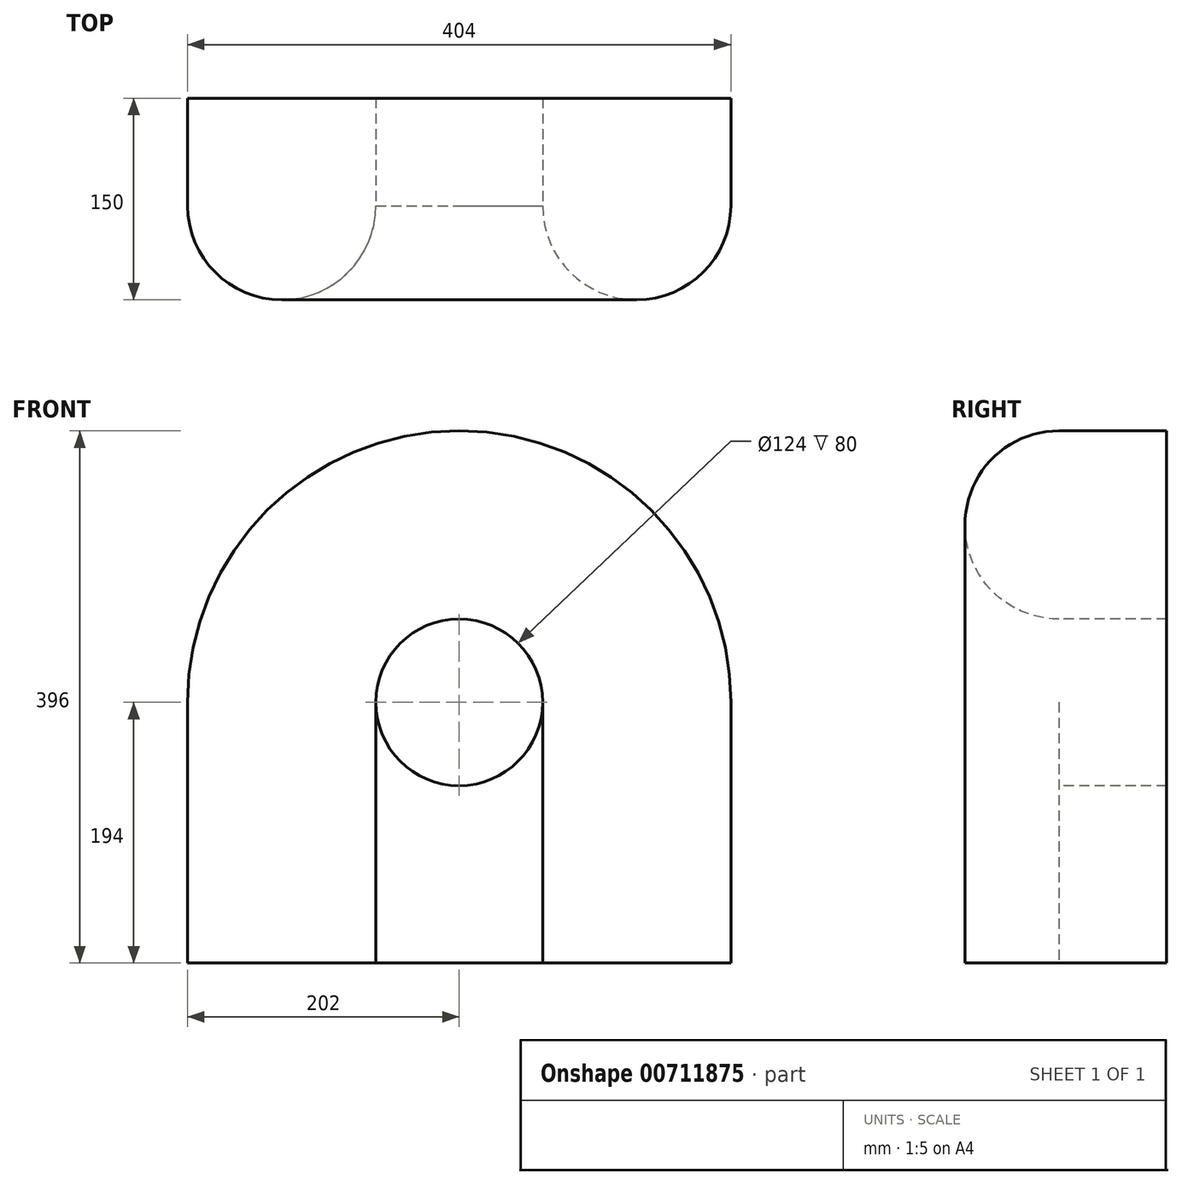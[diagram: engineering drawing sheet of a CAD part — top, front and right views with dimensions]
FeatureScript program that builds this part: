
annotation { "Feature Type Name" : "Feature", "Feature Type Description" : "" }
export const myFeature = defineFeature(function(context is Context, id is Id, definition is map)
    precondition{}
    {
        {
            var Q0;
            Q0=qCreatedBy(makeId("Front.planeOp"),FACE);
            var sketch = newSketch(context, id + "F0", { "sketchPlane" : qUnion([Q0])});
            skLineSegment(sketch, "E0.left", {"start": v(64, 0) * mm, "end": v(64, 194) * mm});
            skLineSegment(sketch, "E0.right", {"start": v(-200, 0) * mm, "end": v(-200, 194) * mm});
            skArc(sketch, "E1", {"start": v(64, 194) * mm, "mid": v(-68, 326) * mm, "end": v(-200, 194) * mm});
            skPoint(sketch, "E1.centerSnap0", {"position": v(-68, 194) * mm});
            skSolve(sketch);
        }
        {
            var Q0;
            Q0=qCreatedBy(makeId("Top.planeOp"),FACE);
            var sketch = newSketch(context, id + "F1", { "sketchPlane" : qUnion([Q0])});
            skCircle(sketch, "E2", {"center": v(64, 0) * mm, "radius": 70 * mm});
            skSolve(sketch);
        }
        {
            var Q0;
            Q0=qCreatedBy(makeId("Front.planeOp"),FACE);
            var sketch = newSketch(context, id + "F2", { "sketchPlane" : qUnion([Q0])});
            skCircle(sketch, "E3", {"center": v(-68, 194) * mm, "radius": 202 * mm});
            skLineSegment(sketch, "E4.bottom", {"start": v(-270, 194) * mm, "end": v(134, 194) * mm});
            skLineSegment(sketch, "E4.top", {"start": v(-270, -18.77) * mm, "end": v(134, -18.77) * mm});
            skLineSegment(sketch, "E4.left", {"start": v(-270, 194) * mm, "end": v(-270, -18.77) * mm});
            skLineSegment(sketch, "E4.right", {"start": v(134, 194) * mm, "end": v(134, -18.77) * mm});
            skSolve(sketch);
        }
        {
            var Q0;
            Q0=makeQuery(id+"F1.imprint","IMPRINT",FACE,{"disambiguationData":[TD([[makeQuery(id+"F1.imprint","IMPRINT",EDGE,{"derivedFrom":sQuery(id+"F1.wireOp",EDGE,"E2")}),1.0]])]});
            var Q1;
            Q1=sQuery(id+"F0.wireOp",EDGE,"E0.left");
            var Q2;
            Q2=sQuery(id+"F0.wireOp",EDGE,"E1");
            var Q3;
            Q3=sQuery(id+"F0.wireOp",EDGE,"E0.right");
            sweep(context, id + "F3", {"profiles" : qUnion([Q0]), "path" : qUnion([Q1, Q2, Q3])});
        }
        {
            var Q0;
            {var subQ0=sQuery(id+"F2.wireOp",EDGE,"E4.bottom");var subQ1=sQuery(id+"F2.wireOp",EDGE,"E3");var subQ3=makeQuery(id+"F2.imprint","INTERSECT",VERTEX,{"derivedFrom":[subQ1,subQ0]});Q0=makeQuery(id+"F2.imprint","IMPRINT",FACE,{"disambiguationData":[TD([[makeQuery(id+"F2.imprint","IMPRINT",EDGE,{"disambiguationData":[TD([[subQ3,-1.0]])],"derivedFrom":subQ1}),1.0]])]});}
            var Q1;
            {var subQ0=sQuery(id+"F2.wireOp",EDGE,"E4.bottom");var subQ1=sQuery(id+"F2.wireOp",EDGE,"E3");var subQ2=makeQuery(id+"F2.imprint","INTERSECT",VERTEX,{"derivedFrom":[subQ1,subQ0]});Q1=makeQuery(id+"F2.imprint","IMPRINT",FACE,{"disambiguationData":[TD([[makeQuery(id+"F2.imprint","IMPRINT",EDGE,{"disambiguationData":[TD([[subQ2,1.0]])],"derivedFrom":subQ1}),1.0]])]});}
            var Q2;
            {var subQ0=sQuery(id+"F2.wireOp",EDGE,"E4.top");Q2=makeQuery(id+"F2.imprint","IMPRINT",FACE,{"disambiguationData":[TD([[makeQuery(id+"F2.imprint","IMPRINT",EDGE,{"derivedFrom":subQ0}),1.0]])]});}
            extrude(context, id + "F4", {"entities" : qUnion([Q0, Q1, Q2]), "operationType" : NewBodyOperationType.ADD, "oppositeDirection" : true, "depth" : 80 * mm, "offsetDistance" : 25 * mm});
        }
        {
            var Q0;
            Q0=qCreatedBy(makeId("Front.planeOp"),FACE);
            var sketch = newSketch(context, id + "F5", { "sketchPlane" : qUnion([Q0])});
            skCircle(sketch, "E5", {"center": v(-68, 194) * mm, "radius": 62 * mm});
            skSolve(sketch);
        }
        {
            var Q0;
            Q0 = qSketchRegion(id + "F5", true);
            extrude(context, id + "F6", {"entities" : qUnion([Q0]), "operationType" : NewBodyOperationType.REMOVE, "oppositeDirection" : true, "depth" : 85 * mm, "offsetDistance" : 25 * mm});
        }
        {
            var Q0;
            Q0=qCreatedBy(makeId("Front.planeOp"),FACE);
            var sketch = newSketch(context, id + "F7", { "sketchPlane" : qUnion([Q0])});
            skLineSegment(sketch, "E6.bottom", {"start": v(-281.4, 0) * mm, "end": v(154.32, 0) * mm});
            skLineSegment(sketch, "E6.top", {"start": v(-281.4, -77.36) * mm, "end": v(154.32, -77.36) * mm});
            skLineSegment(sketch, "E6.left", {"start": v(-281.4, 0) * mm, "end": v(-281.4, -77.36) * mm});
            skLineSegment(sketch, "E6.right", {"start": v(154.32, 0) * mm, "end": v(154.32, -77.36) * mm});
            skSolve(sketch);
        }
        {
            var Q0;
            Q0 = qSketchRegion(id + "F7", true);
            extrude(context, id + "F8", {"entities" : qUnion([Q0]), "operationType" : NewBodyOperationType.REMOVE, "oppositeDirection" : true, "depth" : 80 * mm, "offsetDistance" : 25 * mm});
        }
    });
